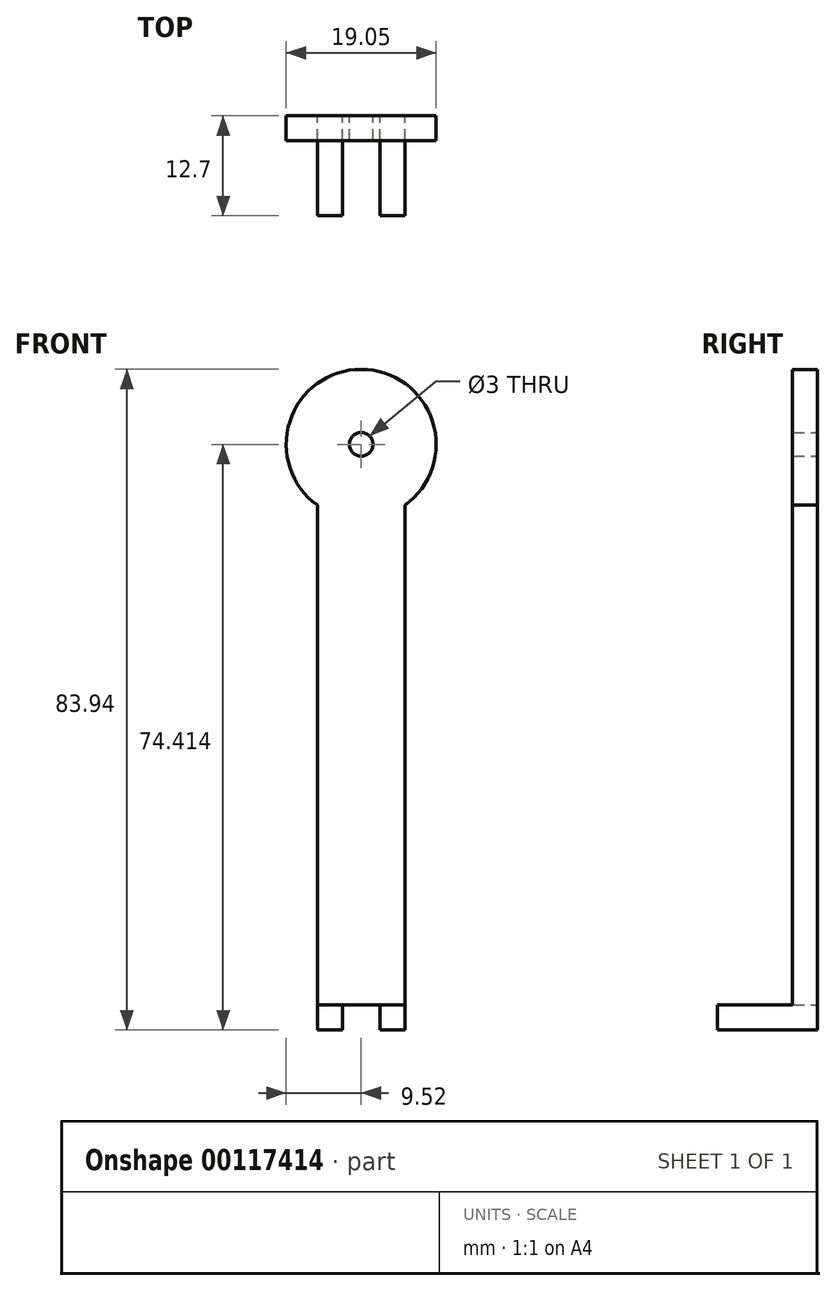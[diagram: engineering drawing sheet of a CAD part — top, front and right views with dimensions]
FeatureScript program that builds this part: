
annotation { "Feature Type Name" : "Feature", "Feature Type Description" : "" }
export const myFeature = defineFeature(function(context is Context, id is Id, definition is map)
    precondition{}
    {
        {
            var Q0;
            Q0=qCreatedBy(makeId("Front.planeOp"),FACE);
            var sketch = newSketch(context, id + "F0", { "sketchPlane" : qUnion([Q0])});
            skCircle(sketch, "E0", {"center": v(-96.84, 34.45) * mm, "radius": 1.5 * mm});
            skArc(sketch, "E1", {"start": v(-91.28, 26.72) * mm, "mid": v(-96.84, 43.98) * mm, "end": v(-102.4, 26.72) * mm});
            skLineSegment(sketch, "E2.top", {"start": v(-102.4, -36.78) * mm, "end": v(-91.28, -36.78) * mm});
            skLineSegment(sketch, "E2.left", {"start": v(-102.4, 26.72) * mm, "end": v(-102.4, -36.78) * mm});
            skLineSegment(sketch, "E2.right", {"start": v(-91.28, 26.72) * mm, "end": v(-91.28, -36.78) * mm});
            skLineSegment(sketch, "E3", {"start": v(-102.4, -36.78) * mm, "end": v(-102.4, -39.96) * mm});
            skLineSegment(sketch, "E4", {"start": v(-102.4, -39.96) * mm, "end": v(-96.05, -39.96) * mm});
            skLineSegment(sketch, "E5", {"start": v(-94.46, -36.78) * mm, "end": v(-94.46, -39.96) * mm});
            skPoint(sketch, "E5.endSnap0", {"position": v(-99.22, -39.96) * mm});
            skLineSegment(sketch, "E6", {"start": v(-99.22, -36.78) * mm, "end": v(-99.22, -39.96) * mm});
            skLineSegment(sketch, "E7", {"start": v(-96.84, 66.6) * mm, "end": v(-96.84, -47.05) * mm, "construction": true});
            skLineSegment(sketch, "E8", {"start": v(-91.28, -36.78) * mm, "end": v(-91.28, -39.96) * mm});
            skLineSegment(sketch, "E9", {"start": v(-91.28, -39.96) * mm, "end": v(-96.05, -39.96) * mm});
            skSolve(sketch);
        }
        {
            var Q0;
            Q0=makeQuery(id+"F0.imprint","IMPRINT",FACE,{"disambiguationData":[TD([[makeQuery(id+"F0.imprint","IMPRINT",EDGE,{"derivedFrom":sQuery(id+"F0.wireOp",EDGE,"E0")}),-1.0]])]});
            extrude(context, id + "F1", {"entities" : qUnion([Q0]), "depth" : 3.17 * mm});
        }
        {
            var Q0;
            {var subQ0=sQuery(id+"F0.wireOp",EDGE,"E3");Q0=makeQuery(id+"F0.imprint","IMPRINT",FACE,{"disambiguationData":[TD([[makeQuery(id+"F0.imprint","IMPRINT",EDGE,{"derivedFrom":subQ0}),1.0]])]});}
            var Q1;
            {var subQ0=sQuery(id+"F0.wireOp",EDGE,"E8");Q1=makeQuery(id+"F0.imprint","IMPRINT",FACE,{"disambiguationData":[TD([[makeQuery(id+"F0.imprint","IMPRINT",EDGE,{"derivedFrom":subQ0}),-1.0]])]});}
            extrude(context, id + "F2", {"entities" : qUnion([Q0, Q1]), "operationType" : NewBodyOperationType.ADD, "depth" : 12.7 * mm});
        }
    });
